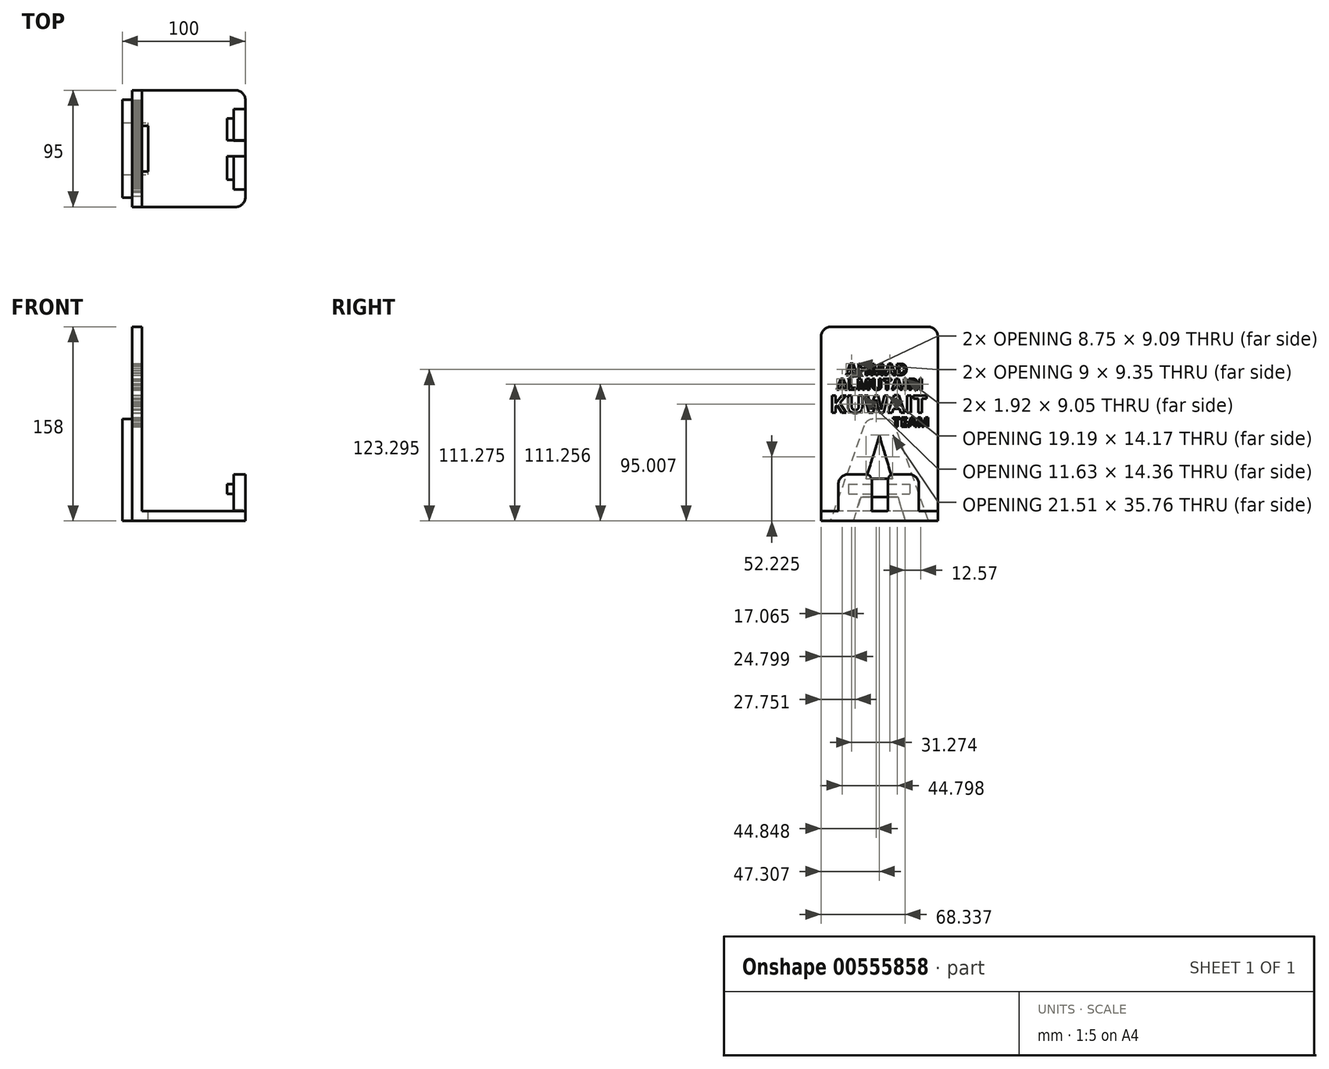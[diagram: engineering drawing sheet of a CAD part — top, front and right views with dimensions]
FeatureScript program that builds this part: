
annotation { "Feature Type Name" : "Feature", "Feature Type Description" : "" }
export const myFeature = defineFeature(function(context is Context, id is Id, definition is map)
    precondition{}
    {
        {
            var Q0;
            Q0=qCreatedBy(makeId("Top.planeOp"),FACE);
            var sketch = newSketch(context, id + "F0", { "sketchPlane" : qUnion([Q0])});
            skLineSegment(sketch, "E0.bottom", {"start": v(-46, -47.5) * mm, "end": v(46, -47.5) * mm});
            skLineSegment(sketch, "E0.top", {"start": v(-46, 47.5) * mm, "end": v(46, 47.5) * mm});
            skLineSegment(sketch, "E0.left", {"start": v(-46, -47.5) * mm, "end": v(-46, 47.5) * mm});
            skLineSegment(sketch, "E0.right", {"start": v(46, -47.5) * mm, "end": v(46, 47.5) * mm});
            skPoint(sketch, "E0.middle", {"position": v(0, 0) * mm});
            skSolve(sketch);
        }
        {
            var Q0;
            Q0=makeQuery(id+"F0.imprint","IMPRINT",FACE,{"disambiguationData":[TD([[makeQuery(id+"F0.imprint","IMPRINT",EDGE,{"derivedFrom":sQuery(id+"F0.wireOp",EDGE,"E0.bottom")}),1.0]])]});
            extrude(context, id + "F1", {"entities" : qUnion([Q0]), "depth" : 8 * mm, "offsetDistance" : 25 * mm});
        }
        {
            var Q0;
            Q0=makeQuery(id+"F1.opExtrude","CAP_FACE",FACE,{"disambiguationData":[OSD([sQuery(id+"F0.wireOp",EDGE,"E0.bottom"),sQuery(id+"F0.wireOp",EDGE,"E0.top"),sQuery(id+"F0.wireOp",EDGE,"E0.left"),sQuery(id+"F0.wireOp",EDGE,"E0.right")])],"isStart":false});
            var sketch = newSketch(context, id + "F2", { "sketchPlane" : qUnion([Q0])});
            skLineSegment(sketch, "E1.bottom", {"start": v(-46, 47.5) * mm, "end": v(-38, 47.5) * mm});
            skLineSegment(sketch, "E1.top", {"start": v(-46, -47.5) * mm, "end": v(-38, -47.5) * mm});
            skLineSegment(sketch, "E1.left", {"start": v(-46, 47.5) * mm, "end": v(-46, -47.5) * mm});
            skLineSegment(sketch, "E1.right", {"start": v(-38, 47.5) * mm, "end": v(-38, -47.5) * mm});
            skSolve(sketch);
        }
        {
            var Q0;
            Q0=qSketchRegion(id+"F2",true);
            extrude(context, id + "F3", {"entities" : qUnion([Q0]), "operationType" : NewBodyOperationType.ADD, "depth" : 150 * mm, "offsetDistance" : 25 * mm});
        }
        {
            var Q0;
            Q0=makeQuery(id+"F1.opExtrude","CAP_FACE",FACE,{"disambiguationData":[OSD([sQuery(id+"F0.wireOp",EDGE,"E0.bottom"),sQuery(id+"F0.wireOp",EDGE,"E0.top"),sQuery(id+"F0.wireOp",EDGE,"E0.left"),sQuery(id+"F0.wireOp",EDGE,"E0.right")])],"isStart":false});
            var sketch = newSketch(context, id + "F4", { "sketchPlane" : qUnion([Q0])});
            skLineSegment(sketch, "E2.bottom", {"start": v(46, 32.06) * mm, "end": v(36.5, 32.06) * mm});
            skLineSegment(sketch, "E2.top", {"start": v(46, -33.37) * mm, "end": v(36.5, -33.37) * mm});
            skLineSegment(sketch, "E2.left", {"start": v(46, 32.06) * mm, "end": v(46, -33.37) * mm});
            skLineSegment(sketch, "E2.right", {"start": v(36.5, 32.06) * mm, "end": v(36.5, -33.37) * mm});
            skSolve(sketch);
        }
        {
            var Q0;
            Q0=makeQuery(id+"F4.imprint","IMPRINT",FACE,{"disambiguationData":[TD([[makeQuery(id+"F4.imprint","IMPRINT",EDGE,{"derivedFrom":sQuery(id+"F4.wireOp",EDGE,"E2.bottom")}),1.0]])]});
            extrude(context, id + "F5", {"entities" : qUnion([Q0]), "operationType" : NewBodyOperationType.ADD, "depth" : 30 * mm, "offsetDistance" : 25 * mm});
        }
        {
            var Q0;
            Q0=makeQuery(id+"F3.boolean.opBoolean","MERGE",FACE,{"derivedFrom":[makeQuery(id+"F1.opExtrude","SWEPT_FACE",FACE,{"disambiguationData":[OSD([sQuery(id+"F0.wireOp",EDGE,"E0.left")])]}),makeQuery(id+"F3.opExtrude","SWEPT_FACE",FACE,{"disambiguationData":[OSD([sQuery(id+"F2.wireOp",EDGE,"E1.left")])]})]});
            var sketch = newSketch(context, id + "F6", { "sketchPlane" : qUnion([Q0])});
            skText(sketch, "E3", { "text": "A", "fontName": "OpenSans-Bold.ttf"});
            const initialGuessF6  = {"E3": [-0.03983, 0, 1, 0, 0.0833]};
            skSetInitialGuess(sketch, initialGuessF6);
            skSolve(sketch);
        }
        {
            var Q0;
            Q0=qSketchRegion(id+"F6",true);
            extrude(context, id + "F7", {"entities" : qUnion([Q0]), "operationType" : NewBodyOperationType.ADD, "depth" : 8 * mm, "offsetDistance" : 25 * mm});
        }
        {
            var Q0;
            Q0=makeQuery(id+"F7.boolean.opBoolean","SPLIT",FACE,{"disambiguationData":[TD([makeQuery(id+"F7.opExtrude","SWEPT_FACE",FACE,{"disambiguationData":[OSD([sQuery(id+"F6.wireOp",EDGE,"E3.sketch_text.stroke-8")])]})])],"derivedFrom":makeQuery(id+"F3.boolean.opBoolean","MERGE",FACE,{"derivedFrom":[makeQuery(id+"F1.opExtrude","SWEPT_FACE",FACE,{"disambiguationData":[OSD([sQuery(id+"F0.wireOp",EDGE,"E0.left")])]}),makeQuery(id+"F3.opExtrude","SWEPT_FACE",FACE,{"disambiguationData":[OSD([sQuery(id+"F2.wireOp",EDGE,"E1.left")])]})]})});
            var Q1;
            {var subQ0=sQuery(id+"F0.wireOp",EDGE,"E0.left");Q1=makeQuery(id+"F7.boolean.opBoolean","SPLIT",FACE,{"disambiguationData":[TD([makeQuery(id+"F7.opExtrude","SWEPT_FACE",FACE,{"disambiguationData":[OSD([sQuery(id+"F6.wireOp",EDGE,"E3.sketch_text.stroke-0")])]})])],"derivedFrom":makeQuery(id+"F3.boolean.opBoolean","MERGE",FACE,{"derivedFrom":[makeQuery(id+"F1.opExtrude","SWEPT_FACE",FACE,{"disambiguationData":[OSD([subQ0])]}),makeQuery(id+"F3.opExtrude","SWEPT_FACE",FACE,{"disambiguationData":[OSD([sQuery(id+"F2.wireOp",EDGE,"E1.left")])]})]})});}
            extrude(context, id + "F8", {"entities" : qUnion([Q0, Q1]), "operationType" : NewBodyOperationType.REMOVE, "oppositeDirection" : true, "depth" : 13 * mm, "offsetDistance" : 25 * mm});
        }
        {
            var Q0;
            Q0=makeQuery(id+"F1.opExtrude","CAP_FACE",FACE,{"disambiguationData":[OSD([sQuery(id+"F0.wireOp",EDGE,"E0.bottom"),sQuery(id+"F0.wireOp",EDGE,"E0.top"),sQuery(id+"F0.wireOp",EDGE,"E0.left"),sQuery(id+"F0.wireOp",EDGE,"E0.right")])],"isStart":false});
            var sketch = newSketch(context, id + "F9", { "sketchPlane" : qUnion([Q0])});
            skLineSegment(sketch, "E4.bottom", {"start": v(-46.36, -6.41) * mm, "end": v(46.36, -6.41) * mm});
            skLineSegment(sketch, "E4.top", {"start": v(-46.36, 6.41) * mm, "end": v(46.36, 6.41) * mm});
            skLineSegment(sketch, "E4.left", {"start": v(-46.36, -6.41) * mm, "end": v(-46.36, 6.41) * mm});
            skLineSegment(sketch, "E4.right", {"start": v(46.36, -6.41) * mm, "end": v(46.36, 6.41) * mm});
            skPoint(sketch, "E4.middle", {"position": v(0, 0) * mm});
            skSolve(sketch);
        }
        {
            var Q0;
            Q0 = qSketchRegion(id + "F9", true);
            extrude(context, id + "F10", {"entities" : qUnion([Q0]), "operationType" : NewBodyOperationType.REMOVE, "depth" : 8 * mm, "offsetDistance" : 25 * mm});
        }
        {
            var Q0;
            Q0=makeQuery(id+"F5.opExtrude","CAP_EDGE",EDGE,{"disambiguationData":[OSD([sQuery(id+"F4.wireOp",EDGE,"E2.top")])],"isStart":false});
            var Q1;
            Q1=makeQuery(id+"F10.boolean.opBoolean","COPY",EDGE,{"derivedFrom":makeQuery(id+"F10.opExtrude","CAP_EDGE",EDGE,{"disambiguationData":[OSD([sQuery(id+"F9.wireOp",EDGE,"E4.bottom")])],"isStart":false})});
            var Q2;
            Q2=makeQuery(id+"F5.opExtrude","CAP_EDGE",EDGE,{"disambiguationData":[OSD([sQuery(id+"F4.wireOp",EDGE,"E2.bottom")])],"isStart":false});
            var Q3;
            Q3=makeQuery(id+"F10.boolean.opBoolean","COPY",EDGE,{"derivedFrom":makeQuery(id+"F10.opExtrude","CAP_EDGE",EDGE,{"disambiguationData":[OSD([sQuery(id+"F9.wireOp",EDGE,"E4.top")])],"isStart":false})});
            var Q4;
            Q4=makeQuery(id+"F1.opExtrude","SWEPT_EDGE",EDGE,{"disambiguationData":[OSD([sQuery(id+"F0.wireOp",EDGE,"E0.bottom"),sQuery(id+"F0.wireOp",EDGE,"E0.right")])]});
            var Q5;
            Q5=makeQuery(id+"F1.opExtrude","SWEPT_EDGE",EDGE,{"disambiguationData":[OSD([sQuery(id+"F0.wireOp",EDGE,"E0.top"),sQuery(id+"F0.wireOp",EDGE,"E0.right")])]});
            var Q6;
            Q6=makeQuery(id+"F3.opExtrude","CAP_EDGE",EDGE,{"disambiguationData":[OSD([sQuery(id+"F2.wireOp",EDGE,"E1.bottom")])],"isStart":false});
            var Q7;
            Q7=makeQuery(id+"F3.opExtrude","CAP_EDGE",EDGE,{"disambiguationData":[OSD([sQuery(id+"F2.wireOp",EDGE,"E1.top")])],"isStart":false});
            var Q8;
            Q8=makeQuery(id+"F7.opExtrude","SWEPT_EDGE",EDGE,{"disambiguationData":[OSD([sQuery(id+"F6.wireOp",EDGE,"E3.sketch_text.stroke-5"),sQuery(id+"F6.wireOp",EDGE,"E3.sketch_text.stroke-6")])]});
            var Q9;
            Q9=makeQuery(id+"F7.opExtrude","SWEPT_EDGE",EDGE,{"disambiguationData":[OSD([sQuery(id+"F6.wireOp",EDGE,"E3.sketch_text.stroke-4"),sQuery(id+"F6.wireOp",EDGE,"E3.sketch_text.stroke-5")])]});
            fillet(context, id + "F11", {"entities" : qUnion([Q0, Q1, Q2, Q3, Q4, Q5, Q6, Q7, Q8, Q9]), "radius" : 8 * mm, "tangentPropagation" : true, "allowEdgeOverflow" : false});
        }
        {
            var Q0;
            Q0=makeQuery(id+"F3.opExtrude","SWEPT_FACE",FACE,{"disambiguationData":[OSD([sQuery(id+"F2.wireOp",EDGE,"E1.right")])]});
            var sketch = newSketch(context, id + "F12", { "sketchPlane" : qUnion([Q0])});
            skSolve(sketch);
        }
        {
            var Q0;
            Q0=makeQuery(id+"F5.boolean.opBoolean","MERGE",FACE,{"derivedFrom":[makeQuery(id+"F1.opExtrude","SWEPT_FACE",FACE,{"disambiguationData":[OSD([sQuery(id+"F0.wireOp",EDGE,"E0.right")])]}),makeQuery(id+"F5.opExtrude","SWEPT_FACE",FACE,{"disambiguationData":[OSD([sQuery(id+"F4.wireOp",EDGE,"E2.left")])]})]});
            var sketch = newSketch(context, id + "F13", { "sketchPlane" : qUnion([Q0])});
            skLineSegment(sketch, "E5.bottom", {"start": v(-25.37, 30) * mm, "end": v(24.63, 30) * mm});
            skLineSegment(sketch, "E5.top", {"start": v(-25.37, 22) * mm, "end": v(24.63, 22) * mm});
            skLineSegment(sketch, "E5.left", {"start": v(-25.37, 30) * mm, "end": v(-25.37, 22) * mm});
            skLineSegment(sketch, "E5.right", {"start": v(24.63, 30) * mm, "end": v(24.63, 22) * mm});
            skSolve(sketch);
        }
        {
            var Q0;
            Q0 = qSketchRegion(id + "F13", true);
            extrude(context, id + "F14", {"entities" : qUnion([Q0]), "operationType" : NewBodyOperationType.ADD, "oppositeDirection" : true, "depth" : 15 * mm, "offsetDistance" : 25 * mm});
        }
        {
            var Q0;
            Q0=qCreatedBy(makeId("Right.planeOp"),FACE);
            var sketch = newSketch(context, id + "F15", { "sketchPlane" : qUnion([Q0])});
            skLineSegment(sketch, "E6.bottom", {"start": v(-6.29, 8.45) * mm, "end": v(6.71, 8.45) * mm});
            skLineSegment(sketch, "E6.top", {"start": v(-6.29, 38.45) * mm, "end": v(6.71, 38.45) * mm});
            skLineSegment(sketch, "E6.left", {"start": v(-6.29, 8.45) * mm, "end": v(-6.29, 38.45) * mm});
            skLineSegment(sketch, "E6.right", {"start": v(6.71, 8.45) * mm, "end": v(6.71, 38.45) * mm});
            skSolve(sketch);
        }
        {
            var Q0;
            Q0 = qSketchRegion(id + "F15", true);
            extrude(context, id + "F16", {"entities" : qUnion([Q0]), "operationType" : NewBodyOperationType.REMOVE, "depth" : 51 * mm, "offsetDistance" : 25 * mm});
        }
        {
            var Q0;
            Q0=makeQuery(id+"F16.boolean.opBoolean","INTERSECT",EDGE,{"derivedFrom":[makeQuery(id+"F5.opExtrude","CAP_FACE",FACE,{"disambiguationData":[OSD([sQuery(id+"F4.wireOp",EDGE,"E2.bottom"),sQuery(id+"F4.wireOp",EDGE,"E2.top"),sQuery(id+"F4.wireOp",EDGE,"E2.left"),sQuery(id+"F4.wireOp",EDGE,"E2.right")])],"isStart":false}),makeQuery(id+"F16.opExtrude","SWEPT_FACE",FACE,{"disambiguationData":[OSD([sQuery(id+"F15.wireOp",EDGE,"E6.left")])]})]});
            var Q1;
            Q1=makeQuery(id+"F16.boolean.opBoolean","INTERSECT",EDGE,{"derivedFrom":[makeQuery(id+"F5.opExtrude","CAP_FACE",FACE,{"disambiguationData":[OSD([sQuery(id+"F4.wireOp",EDGE,"E2.bottom"),sQuery(id+"F4.wireOp",EDGE,"E2.top"),sQuery(id+"F4.wireOp",EDGE,"E2.left"),sQuery(id+"F4.wireOp",EDGE,"E2.right")])],"isStart":false}),makeQuery(id+"F16.opExtrude","SWEPT_FACE",FACE,{"disambiguationData":[OSD([sQuery(id+"F15.wireOp",EDGE,"E6.right")])]})]});
            fillet(context, id + "F17", {"entities" : qUnion([Q0, Q1]), "radius" : 5 * mm, "tangentPropagation" : true, "allowEdgeOverflow" : false});
        }
        {
            var Q0;
            {var subQ0=sQuery(id+"F2.wireOp",EDGE,"E1.right");Q0=makeQuery(id+"F12.imprint","IMPRINT",FACE,{"disambiguationData":[TD([[makeQuery(id+"F12.imprint","IMPRINT",EDGE,{"derivedFrom":makeQuery(id+"F3.opExtrude","CAP_EDGE",EDGE,{"disambiguationData":[OSD([subQ0])],"isStart":false})}),1.0]])]});}
            var sketch = newSketch(context, id + "F18", { "sketchPlane" : qUnion([Q0])});
            skText(sketch, "E7", { "text": "KUWAIT", "fontName": "OpenSans-Bold.ttf"});
            const initialGuessF18  = {"E7": [-0.04043, 0.08802, 1, 0, 0.01429]};
            skSetInitialGuess(sketch, initialGuessF18);
            skSolve(sketch);
        }
        {
            var Q0;
            {var subQ0=sQuery(id+"F2.wireOp",EDGE,"E1.right");Q0=makeQuery(id+"F12.imprint","IMPRINT",FACE,{"disambiguationData":[TD([[makeQuery(id+"F12.imprint","IMPRINT",EDGE,{"derivedFrom":makeQuery(id+"F3.opExtrude","CAP_EDGE",EDGE,{"disambiguationData":[OSD([subQ0])],"isStart":false})}),1.0]])]});}
            var sketch = newSketch(context, id + "F19", { "sketchPlane" : qUnion([Q0])});
            skText(sketch, "E8", { "text": "TEAM", "fontName": "OpenSans-Bold.ttf"});
            const initialGuessF19  = {"E8": [0.01073, 0.07663, 1, 0, 0.00774]};
            skSetInitialGuess(sketch, initialGuessF19);
            skSolve(sketch);
        }
        {
            var Q0;
            {var subQ0=sQuery(id+"F2.wireOp",EDGE,"E1.right");Q0=makeQuery(id+"F12.imprint","IMPRINT",FACE,{"disambiguationData":[TD([[makeQuery(id+"F12.imprint","IMPRINT",EDGE,{"derivedFrom":makeQuery(id+"F3.opExtrude","CAP_EDGE",EDGE,{"disambiguationData":[OSD([subQ0])],"isStart":false})}),1.0]])]});}
            var sketch = newSketch(context, id + "F20", { "sketchPlane" : qUnion([Q0])});
            skText(sketch, "E9", { "text": "AHMAD\n", "fontName": "OpenSans-Bold.ttf"});
            const initialGuessF20  = {"E9": [-0.0272, 0.11862, 1, 0, 0.00939]};
            skSetInitialGuess(sketch, initialGuessF20);
            skSolve(sketch);
        }
        {
            var Q0;
            {var subQ0=sQuery(id+"F2.wireOp",EDGE,"E1.right");Q0=makeQuery(id+"F12.imprint","IMPRINT",FACE,{"disambiguationData":[TD([[makeQuery(id+"F12.imprint","IMPRINT",EDGE,{"derivedFrom":makeQuery(id+"F3.opExtrude","CAP_EDGE",EDGE,{"disambiguationData":[OSD([subQ0])],"isStart":false})}),1.0]])]});}
            var sketch = newSketch(context, id + "F21", { "sketchPlane" : qUnion([Q0])});
            skText(sketch, "E10", { "text": "ALMUTAIRI", "fontName": "OpenSans-Bold.ttf"});
            const initialGuessF21  = {"E10": [-0.03481, 0.10673, 1, 0, 0.00913]};
            skSetInitialGuess(sketch, initialGuessF21);
            skSolve(sketch);
        }
        {
            var Q0;
            Q0 = qSketchRegion(id + "F21", true);
            var Q1;
            Q1 = qSketchRegion(id + "F18", true);
            var Q2;
            Q2 = qSketchRegion(id + "F19", true);
            var Q3;
            Q3 = qSketchRegion(id + "F20", true);
            extrude(context, id + "F22", {"entities" : qUnion([Q0, Q1, Q2, Q3]), "operationType" : NewBodyOperationType.REMOVE, "oppositeDirection" : true, "depth" : 25 * mm, "offsetDistance" : 25 * mm});
        }
    });
